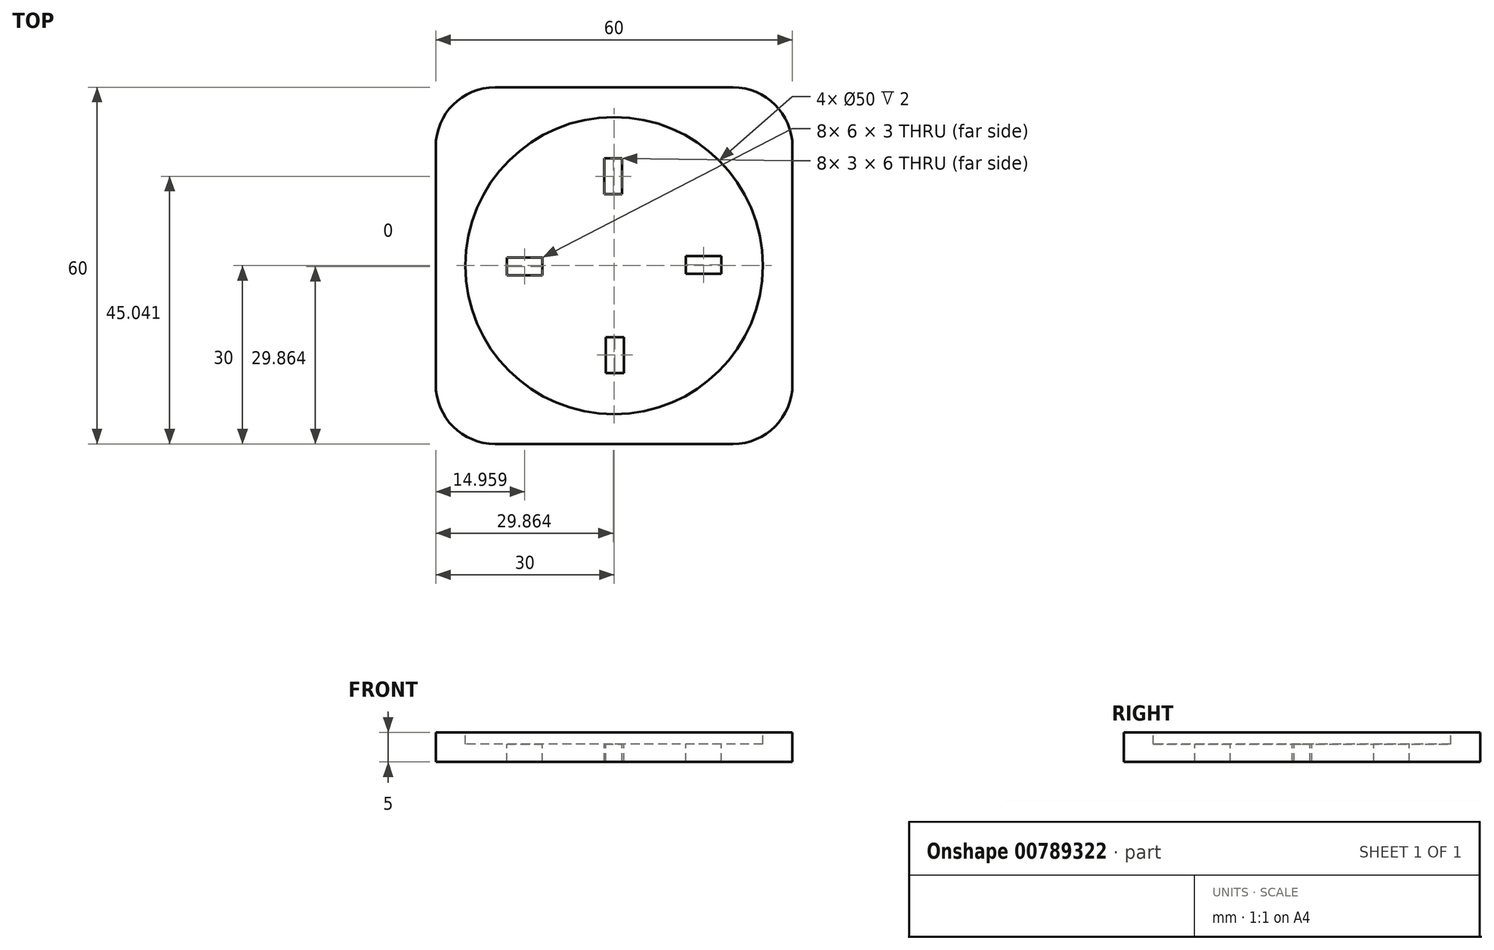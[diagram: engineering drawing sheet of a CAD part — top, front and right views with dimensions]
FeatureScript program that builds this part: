
annotation { "Feature Type Name" : "Feature", "Feature Type Description" : "" }
export const myFeature = defineFeature(function(context is Context, id is Id, definition is map)
    precondition{}
    {
        {
            var Q0;
            Q0=qCreatedBy(makeId("Top.planeOp"),FACE);
            var sketch = newSketch(context, id + "F0", { "sketchPlane" : qUnion([Q0])});
            skLineSegment(sketch, "E0.bottom", {"start": v(30, 30) * mm, "end": v(-30, 30) * mm});
            skLineSegment(sketch, "E0.top", {"start": v(30, -30) * mm, "end": v(-30, -30) * mm});
            skLineSegment(sketch, "E0.left", {"start": v(30, 30) * mm, "end": v(30, -30) * mm});
            skLineSegment(sketch, "E0.right", {"start": v(-30, 30) * mm, "end": v(-30, -30) * mm});
            skPoint(sketch, "E0.middle", {"position": v(0, 0) * mm});
            skSolve(sketch);
        }
        {
            var Q0;
            Q0=makeQuery(id+"F0.imprint","IMPRINT",FACE,{"disambiguationData":[TD([[makeQuery(id+"F0.imprint","IMPRINT",EDGE,{"derivedFrom":sQuery(id+"F0.wireOp",EDGE,"E0.bottom")}),1.0]])]});
            extrude(context, id + "F1", {"entities" : qUnion([Q0]), "depth" : 5 * mm, "offsetDistance" : 25 * mm});
        }
        {
            var Q0;
            Q0=makeQuery(id+"F1.opExtrude","CAP_FACE",FACE,{"disambiguationData":[OSD([sQuery(id+"F0.wireOp",EDGE,"E0.bottom"),sQuery(id+"F0.wireOp",EDGE,"E0.top"),sQuery(id+"F0.wireOp",EDGE,"E0.left"),sQuery(id+"F0.wireOp",EDGE,"E0.right")])],"isStart":false});
            var sketch = newSketch(context, id + "F2", { "sketchPlane" : qUnion([Q0])});
            skCircle(sketch, "E1", {"center": v(0, 0) * mm, "radius": 25 * mm});
            skSolve(sketch);
        }
        {
            var Q0;
            Q0=makeQuery(id+"F2.imprint","IMPRINT",FACE,{"disambiguationData":[TD([[makeQuery(id+"F2.imprint","IMPRINT",EDGE,{"derivedFrom":sQuery(id+"F2.wireOp",EDGE,"E1")}),1.0]])]});
            extrude(context, id + "F3", {"entities" : qUnion([Q0]), "operationType" : NewBodyOperationType.REMOVE, "oppositeDirection" : true, "depth" : 2 * mm, "offsetDistance" : 25 * mm});
        }
        {
            var Q0;
            Q0=makeQuery(id+"F1.opExtrude","SWEPT_EDGE",EDGE,{"disambiguationData":[OSD([sQuery(id+"F0.wireOp",EDGE,"E0.bottom"),sQuery(id+"F0.wireOp",EDGE,"E0.right")])]});
            var Q1;
            Q1=makeQuery(id+"F1.opExtrude","SWEPT_EDGE",EDGE,{"disambiguationData":[OSD([sQuery(id+"F0.wireOp",EDGE,"E0.bottom"),sQuery(id+"F0.wireOp",EDGE,"E0.left")])]});
            var Q2;
            Q2=makeQuery(id+"F1.opExtrude","SWEPT_EDGE",EDGE,{"disambiguationData":[OSD([sQuery(id+"F0.wireOp",EDGE,"E0.top"),sQuery(id+"F0.wireOp",EDGE,"E0.left")])]});
            var Q3;
            Q3=makeQuery(id+"F1.opExtrude","SWEPT_EDGE",EDGE,{"disambiguationData":[OSD([sQuery(id+"F0.wireOp",EDGE,"E0.top"),sQuery(id+"F0.wireOp",EDGE,"E0.right")])]});
            fillet(context, id + "F4", {"entities" : qUnion([Q0, Q1, Q2, Q3]), "radius" : 10 * mm, "tangentPropagation" : true, "allowEdgeOverflow" : false});
        }
        {
            var Q0;
            Q0=makeQuery(id+"F3.boolean.opBoolean","COPY",FACE,{"derivedFrom":makeQuery(id+"F3.opExtrude","CAP_FACE",FACE,{"disambiguationData":[OSD([sQuery(id+"F2.wireOp",EDGE,"E1")])],"isStart":false})});
            var sketch = newSketch(context, id + "F5", { "sketchPlane" : qUnion([Q0])});
            skLineSegment(sketch, "E2.bottom", {"start": v(-1.64, 18.04) * mm, "end": v(1.36, 18.04) * mm});
            skLineSegment(sketch, "E2.top", {"start": v(-1.64, 12.04) * mm, "end": v(1.36, 12.04) * mm});
            skLineSegment(sketch, "E2.left", {"start": v(-1.64, 18.04) * mm, "end": v(-1.64, 12.04) * mm});
            skLineSegment(sketch, "E2.right", {"start": v(1.36, 18.04) * mm, "end": v(1.36, 12.04) * mm});
            skLineSegment(sketch, "E3.1.0", {"start": v(-18.04, -1.64) * mm, "end": v(-18.04, 1.36) * mm});
            skLineSegment(sketch, "E3.1.1", {"start": v(-18.04, -1.64) * mm, "end": v(-12.04, -1.64) * mm});
            skLineSegment(sketch, "E3.1.2", {"start": v(-12.04, -1.64) * mm, "end": v(-12.04, 1.36) * mm});
            skLineSegment(sketch, "E3.1.3", {"start": v(-18.04, 1.36) * mm, "end": v(-12.04, 1.36) * mm});
            skLineSegment(sketch, "E3.2.0", {"start": v(1.64, -18.04) * mm, "end": v(-1.36, -18.04) * mm});
            skLineSegment(sketch, "E3.2.1", {"start": v(1.64, -18.04) * mm, "end": v(1.64, -12.04) * mm});
            skLineSegment(sketch, "E3.2.2", {"start": v(1.64, -12.04) * mm, "end": v(-1.36, -12.04) * mm});
            skLineSegment(sketch, "E3.2.3", {"start": v(-1.36, -18.04) * mm, "end": v(-1.36, -12.04) * mm});
            skLineSegment(sketch, "E3.3.0", {"start": v(18.04, 1.64) * mm, "end": v(18.04, -1.36) * mm});
            skLineSegment(sketch, "E3.3.1", {"start": v(18.04, 1.64) * mm, "end": v(12.04, 1.64) * mm});
            skLineSegment(sketch, "E3.3.2", {"start": v(12.04, 1.64) * mm, "end": v(12.04, -1.36) * mm});
            skLineSegment(sketch, "E3.3.3", {"start": v(18.04, -1.36) * mm, "end": v(12.04, -1.36) * mm});
            skPoint(sketch, "E3.center", {"position": v(0, 0) * mm});
            skSolve(sketch);
        }
        {
            var Q0;
            Q0=makeQuery(id+"F5.imprint","IMPRINT",FACE,{"disambiguationData":[TD([[makeQuery(id+"F5.imprint","IMPRINT",EDGE,{"derivedFrom":sQuery(id+"F5.wireOp",EDGE,"E3.1.0")}),-1.0]])]});
            var Q1;
            Q1=makeQuery(id+"F5.imprint","IMPRINT",FACE,{"disambiguationData":[TD([[makeQuery(id+"F5.imprint","IMPRINT",EDGE,{"derivedFrom":sQuery(id+"F5.wireOp",EDGE,"E2.bottom")}),-1.0]])]});
            var Q2;
            Q2=makeQuery(id+"F5.imprint","IMPRINT",FACE,{"disambiguationData":[TD([[makeQuery(id+"F5.imprint","IMPRINT",EDGE,{"derivedFrom":sQuery(id+"F5.wireOp",EDGE,"E3.2.0")}),-1.0]])]});
            var Q3;
            Q3=makeQuery(id+"F5.imprint","IMPRINT",FACE,{"disambiguationData":[TD([[makeQuery(id+"F5.imprint","IMPRINT",EDGE,{"derivedFrom":sQuery(id+"F5.wireOp",EDGE,"E3.3.0")}),-1.0]])]});
            extrude(context, id + "F6", {"entities" : qUnion([Q0, Q1, Q2, Q3]), "operationType" : NewBodyOperationType.REMOVE, "oppositeDirection" : true, "depth" : 25 * mm, "offsetDistance" : 25 * mm});
        }
    });
